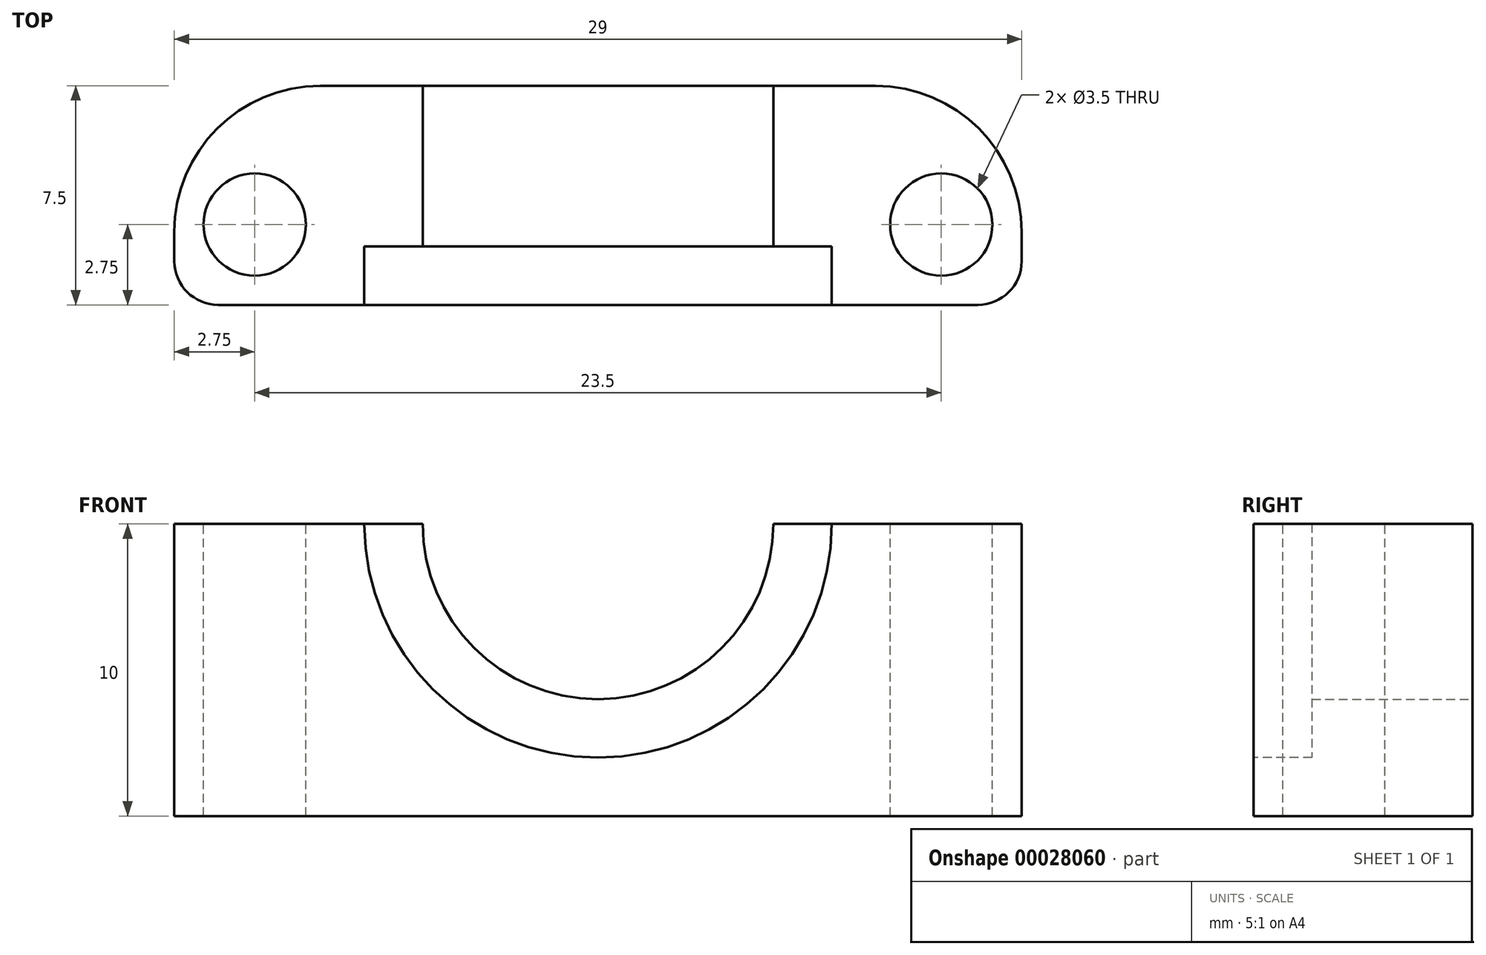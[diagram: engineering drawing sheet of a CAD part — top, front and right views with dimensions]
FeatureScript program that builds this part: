
annotation { "Feature Type Name" : "Feature", "Feature Type Description" : "" }
export const myFeature = defineFeature(function(context is Context, id is Id, definition is map)
    precondition{}
    {
        {
            var Q0;
            Q0=qCreatedBy(makeId("Top.planeOp"),FACE);
            var sketch = newSketch(context, id + "F0", { "sketchPlane" : qUnion([Q0])});
            skLineSegment(sketch, "E0.bottom", {"start": v(0, 0) * mm, "end": v(25, 0) * mm});
            skLineSegment(sketch, "E0.top", {"start": v(0, 11) * mm, "end": v(25, 11) * mm});
            skLineSegment(sketch, "E0.left", {"start": v(0, 0) * mm, "end": v(0, 11) * mm});
            skLineSegment(sketch, "E0.right", {"start": v(25, 0) * mm, "end": v(25, 11) * mm});
            skSolve(sketch);
        }
        {
            var Q0;
            Q0=qSketchRegion(id+"F0",true);
            extrude(context, id + "F1", {"entities" : qUnion([Q0]), "depth" : 10 * mm});
        }
        {
            var Q0;
            Q0=makeQuery(id+"F1.opExtrude","SWEPT_FACE",FACE,{"disambiguationData":[OSD([sQuery(id+"F0.wireOp",EDGE,"E0.bottom")])]});
            var sketch = newSketch(context, id + "F2", { "sketchPlane" : qUnion([Q0])});
            skCircle(sketch, "E1", {"center": v(12.5, 10) * mm, "radius": 8 * mm});
            skSolve(sketch);
        }
        {
            var Q0;
            Q0=qSketchRegion(id+"F2",true);
            extrude(context, id + "F3", {"entities" : qUnion([Q0]), "operationType" : NewBodyOperationType.REMOVE, "oppositeDirection" : true, "depth" : 5.5 * mm});
        }
        {
            var Q0;
            Q0=makeQuery(id+"F1.opExtrude","SWEPT_FACE",FACE,{"disambiguationData":[OSD([sQuery(id+"F0.wireOp",EDGE,"E0.top")])]});
            var sketch = newSketch(context, id + "F4", { "sketchPlane" : qUnion([Q0])});
            skCircle(sketch, "E2", {"center": v(-12.5, 10) * mm, "radius": 6 * mm});
            skSolve(sketch);
        }
        {
            var Q0;
            Q0=qSketchRegion(id+"F4",true);
            extrude(context, id + "F5", {"entities" : qUnion([Q0]), "operationType" : NewBodyOperationType.REMOVE, "oppositeDirection" : true, "depth" : 6 * mm});
        }
        {
            var Q0;
            Q0=makeQuery(id+"F1.opExtrude","SWEPT_FACE",FACE,{"disambiguationData":[OSD([sQuery(id+"F0.wireOp",EDGE,"E0.left")])]});
            var sketch = newSketch(context, id + "F6", { "sketchPlane" : qUnion([Q0])});
            skLineSegment(sketch, "E3.bottom", {"start": v(-11, 0) * mm, "end": v(0, 0) * mm});
            skLineSegment(sketch, "E3.top", {"start": v(-11, 10) * mm, "end": v(0, 10) * mm});
            skLineSegment(sketch, "E3.left", {"start": v(-11, 0) * mm, "end": v(-11, 10) * mm});
            skLineSegment(sketch, "E3.right", {"start": v(0, 0) * mm, "end": v(0, 10) * mm});
            skSolve(sketch);
        }
        {
            var Q0;
            Q0=qSketchRegion(id+"F6",true);
            extrude(context, id + "F7", {"entities" : qUnion([Q0]), "operationType" : NewBodyOperationType.ADD, "depth" : 2 * mm});
        }
        {
            var Q0;
            Q0=makeQuery(id+"F1.opExtrude","SWEPT_FACE",FACE,{"disambiguationData":[OSD([sQuery(id+"F0.wireOp",EDGE,"E0.right")])]});
            var sketch = newSketch(context, id + "F8", { "sketchPlane" : qUnion([Q0])});
            skLineSegment(sketch, "E4.bottom", {"start": v(11, 10) * mm, "end": v(0, 10) * mm});
            skLineSegment(sketch, "E4.top", {"start": v(11, 0) * mm, "end": v(0, 0) * mm});
            skLineSegment(sketch, "E4.left", {"start": v(11, 10) * mm, "end": v(11, 0) * mm});
            skLineSegment(sketch, "E4.right", {"start": v(0, 10) * mm, "end": v(0, 0) * mm});
            skSolve(sketch);
        }
        {
            var Q0;
            Q0=qSketchRegion(id+"F8",true);
            extrude(context, id + "F9", {"entities" : qUnion([Q0]), "operationType" : NewBodyOperationType.ADD, "depth" : 2 * mm});
        }
        {
            var Q0;
            Q0=makeQuery(id+"F9.opExtrude","CAP_EDGE",EDGE,{"disambiguationData":[OSD([sQuery(id+"F8.wireOp",EDGE,"E4.left")])],"isStart":false});
            var Q1;
            Q1=makeQuery(id+"F9.opExtrude","CAP_EDGE",EDGE,{"disambiguationData":[OSD([sQuery(id+"F8.wireOp",EDGE,"E4.right")])],"isStart":false});
            var Q2;
            Q2=makeQuery(id+"F7.opExtrude","CAP_EDGE",EDGE,{"disambiguationData":[OSD([sQuery(id+"F6.wireOp",EDGE,"E3.left")])],"isStart":false});
            var Q3;
            Q3=makeQuery(id+"F7.opExtrude","CAP_EDGE",EDGE,{"disambiguationData":[OSD([sQuery(id+"F6.wireOp",EDGE,"E3.right")])],"isStart":false});
            fillet(context, id + "F10", {"entities" : qUnion([Q0, Q1, Q2, Q3]), "radius" : 5 * mm, "tangentPropagation" : true, "allowEdgeOverflow" : false});
        }
        {
            var Q0;
            {var subQ0=sQuery(id+"F0.wireOp",EDGE,"E0.bottom");var subQ1=sQuery(id+"F0.wireOp",EDGE,"E0.top");var subQ2=sQuery(id+"F0.wireOp",EDGE,"E0.left");Q0=makeQuery(id+"F5.boolean.opBoolean","SPLIT",FACE,{"disambiguationData":[TD([makeQuery(id+"F1.opExtrude","SWEPT_FACE",FACE,{"disambiguationData":[OSD([subQ2])]})])],"derivedFrom":makeQuery(id+"F1.opExtrude","CAP_FACE",FACE,{"disambiguationData":[OSD([subQ0,subQ1,subQ2,sQuery(id+"F0.wireOp",EDGE,"E0.right")])],"isStart":false})});}
            var sketch = newSketch(context, id + "F11", { "sketchPlane" : qUnion([Q0])});
            skCircle(sketch, "E5", {"center": v(0.75, 6.25) * mm, "radius": 1.75 * mm});
            skCircle(sketch, "E6", {"center": v(24.25, 6.25) * mm, "radius": 1.75 * mm});
            skSolve(sketch);
        }
        {
            var Q0;
            Q0=qSketchRegion(id+"F11",true);
            extrude(context, id + "F12", {"entities" : qUnion([Q0]), "operationType" : NewBodyOperationType.REMOVE, "oppositeDirection" : true, "depth" : 25 * mm});
        }
        {
            var Q0;
            {var subQ1=sQuery(id+"F0.wireOp",EDGE,"E0.left");var subQ2=sQuery(id+"F0.wireOp",EDGE,"E0.top");var subQ3=sQuery(id+"F0.wireOp",EDGE,"E0.bottom");Q0=makeQuery(id+"F7.boolean.opBoolean","MERGE",FACE,{"derivedFrom":[makeQuery(id+"F5.boolean.opBoolean","SPLIT",FACE,{"disambiguationData":[TD([makeQuery(id+"F1.opExtrude","SWEPT_FACE",FACE,{"disambiguationData":[OSD([subQ1])]})])],"derivedFrom":makeQuery(id+"F1.opExtrude","CAP_FACE",FACE,{"disambiguationData":[OSD([subQ3,subQ2,subQ1,sQuery(id+"F0.wireOp",EDGE,"E0.right")])],"isStart":false})}),makeQuery(id+"F7.opExtrude","SWEPT_FACE",FACE,{"disambiguationData":[OSD([sQuery(id+"F6.wireOp",EDGE,"E3.top")])]})]});}
            var sketch = newSketch(context, id + "F13", { "sketchPlane" : qUnion([Q0])});
            skLineSegment(sketch, "E7.bottom", {"start": v(-4.97, 3.5) * mm, "end": v(34.53, 3.5) * mm});
            skLineSegment(sketch, "E7.top", {"start": v(-4.97, 0) * mm, "end": v(34.53, 0) * mm});
            skLineSegment(sketch, "E7.left", {"start": v(-4.97, 3.5) * mm, "end": v(-4.97, 0) * mm});
            skLineSegment(sketch, "E7.right", {"start": v(34.53, 3.5) * mm, "end": v(34.53, 0) * mm});
            skSolve(sketch);
        }
        {
            var Q0;
            Q0 = qSketchRegion(id + "F13", true);
            extrude(context, id + "F14", {"entities" : qUnion([Q0]), "operationType" : NewBodyOperationType.REMOVE, "oppositeDirection" : true, "depth" : 25 * mm});
        }
        {
            var Q0;
            Q0=makeQuery(id+"F14.boolean.opBoolean","INTERSECT",EDGE,{"derivedFrom":[makeQuery(id+"F10.opFillet","BLEND_FACE",FACE,{"disambiguationData":[OSD([sQuery(id+"F8.wireOp",EDGE,"E4.right")])]}),makeQuery(id+"F14.opExtrude","SWEPT_FACE",FACE,{"disambiguationData":[OSD([sQuery(id+"F13.wireOp",EDGE,"E7.bottom")])]})]});
            var Q1;
            Q1=makeQuery(id+"F14.boolean.opBoolean","INTERSECT",EDGE,{"derivedFrom":[makeQuery(id+"F10.opFillet","BLEND_FACE",FACE,{"disambiguationData":[OSD([sQuery(id+"F6.wireOp",EDGE,"E3.right")])]}),makeQuery(id+"F14.opExtrude","SWEPT_FACE",FACE,{"disambiguationData":[OSD([sQuery(id+"F13.wireOp",EDGE,"E7.bottom")])]})]});
            fillet(context, id + "F15", {"entities" : qUnion([Q0, Q1]), "radius" : 1.5 * mm, "tangentPropagation" : true, "allowEdgeOverflow" : false});
        }
    });
